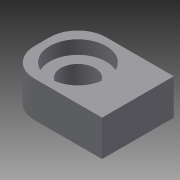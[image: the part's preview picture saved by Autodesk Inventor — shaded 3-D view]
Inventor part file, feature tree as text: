
AUTODESK INVENTOR PART (.ipt)
format: ipt  version: 2013 (Build 170138000, 138)  size: 100,864 bytes
history: native  units: in
note: dims shown in document units (in); Inventor stores cm internally (conversion verified against a paired STEP export)
features: extrude x3, sketch x3, fillet x1
ambient origin geometry x8: Origin, YZ Plane, XZ Plane, XY Plane, X Axis, Y Axis, Z Axis, Center Point
bodies: Solid1 (feature_tree)
feature tree (7):
  extrude  "Extrusion1"  Depth=1.5in
  extrude  "Extrusion2"  Depth=1.1811in
  extrude  "Extrusion3"  Depth=0.75in
  fillet  "Fillet1"  Radius=0.2812in
  sketch  "Sketch1"  dims[d0=2.005in d1=1.5in]
  sketch  "Sketch2"  dims[d2=0.75in d3=0.0in d4=1.1811in]
  sketch  "Sketch3"  dims[d5=0.75in d6=0.75in d7=0.2812in d8=0.0in d9=0.25in d10=0.2812in d11=0.0in d12=0.2328in d13=0.2328in d14=0.5906in d15=0.75in]
